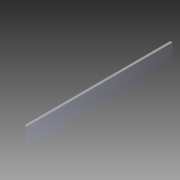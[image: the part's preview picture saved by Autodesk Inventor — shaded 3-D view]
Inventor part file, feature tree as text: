
AUTODESK INVENTOR PART (.ipt)
format: ipt  version: 2012 (Build 160160000, 160)  size: 90,112 bytes
history: native  units: in
note: dims shown in document units (in); Inventor stores cm internally (conversion verified against a paired STEP export)
features: extrude x3, sketch x3
ambient origin geometry x8: Origin, YZ Plane, XZ Plane, XY Plane, X Axis, Y Axis, Z Axis, Center Point
bodies: Solid1 (feature_tree)
feature tree (6):
  extrude  "Extrusion1"  Depth=1.0in
  extrude  "Extrusion2"  Depth=0.125in
  extrude  "Extrusion3"  TaperAngle=45.0deg  [1 undecoded]
  sketch  "Sketch1"  dims[d0=1.0in d1=1.0in]
  sketch  "Sketch2"  dims[d2=0.125in d3=0.125in]
  sketch  "Sketch3"  dims[d4=8.125in d5=0.0in d6=45.0deg d7=7.0in d8=0.0in d9=0.25in d10=4.5in d11=0.375in d12=1.0in d13=0.0in]
note: 1 required parameter value undecoded (feature->parameter linkage not recoverable at this tier; creation-order binding heuristic only, values carry confidence <= 0.55)
